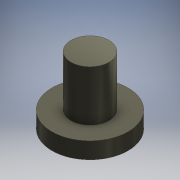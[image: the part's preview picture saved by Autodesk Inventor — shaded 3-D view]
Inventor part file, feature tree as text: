
AUTODESK INVENTOR PART (.ipt)
format: ipt  version: 2016 (Build 200138000, 138)  size: 99,328 bytes
history: native  units: mm
features: extrude x2, other x1, sketch x1
ambient origin geometry x8: Origin, YZ Plane, XZ Plane, XY Plane, X Axis, Y Axis, Z Axis, Center Point
bodies: Body1 (feature_tree)
feature tree (4):
  other  "ソリッド1"
  sketch  "スケッチ1"
  extrude  "押し出し1"  Depth=6.0mm
  extrude  "押し出し2"  Depth=3.0mm
